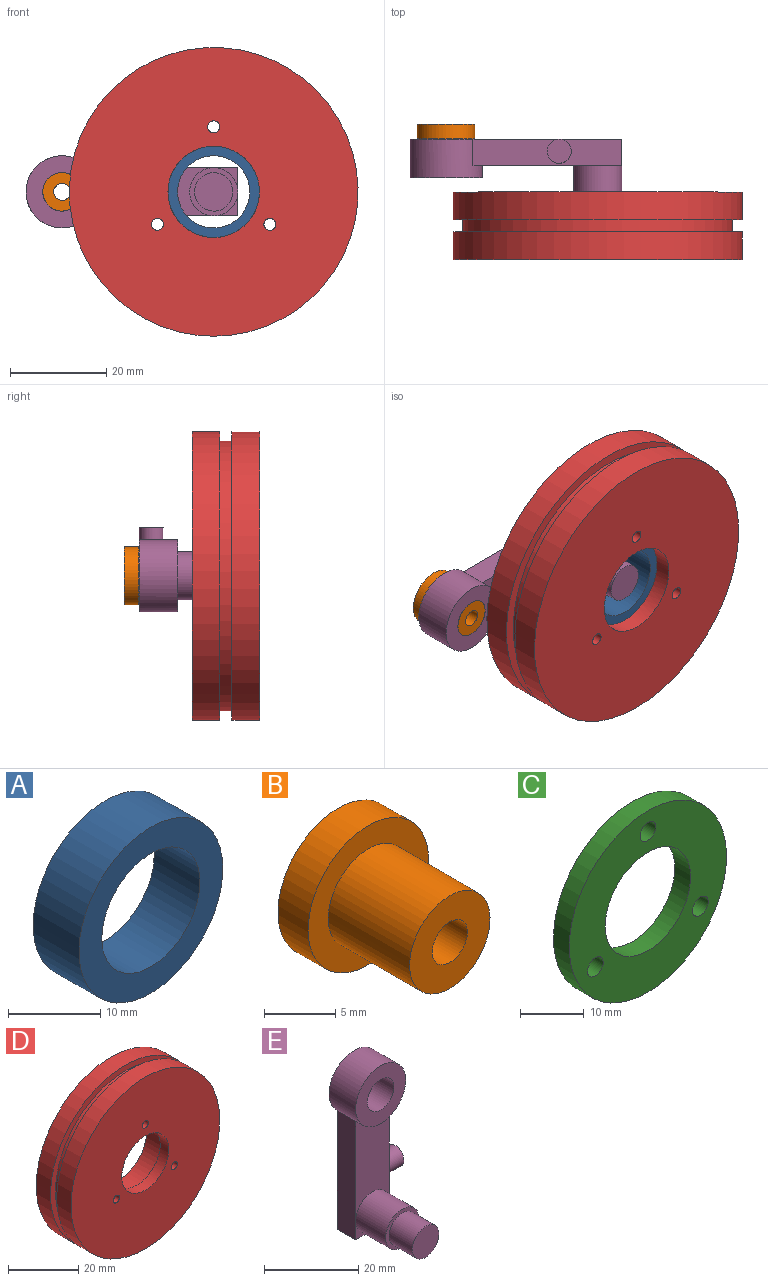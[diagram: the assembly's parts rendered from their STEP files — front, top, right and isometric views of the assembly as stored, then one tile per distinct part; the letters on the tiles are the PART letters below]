
ASSEMBLY  parts=5 mates=7
PART A: 4 faces, bbox 22x7x22 mm
  f0: cylinder r=7.5mm len=15mm, axis (0,1,0), area 329.9mm2, adj f2,f3
  f1: cylinder r=11mm len=22mm, axis (0,1,0), area 483.8mm2, adj f2,f3
  f2: plane 22x22mm, normal (0,-1,0), area 203.4mm2, adj f0,f1
  f3: plane 22x22mm, normal (0,1,0), area 203.4mm2, adj f0,f1
PART B: 6 faces, bbox 12x11.1x12 mm
  f0: cylinder r=4mm len=8.1mm, axis (0,1,0), area 203.6mm2, adj f1,f4
  f1: plane 8x8mm, normal (0,-1,0), area 40.6mm2, adj f0,f5
  f2: cylinder r=6mm len=12mm, axis (0,-1,0), area 113.1mm2, adj f3,f4
  f3: plane 12x12mm, normal (0,1,0), area 103.5mm2, adj f2,f5
  f4: plane 12x12mm, normal (0,-1,0), area 62.8mm2, adj f0,f2
  f5: cylinder r=1.75mm len=11.1mm, axis (0,-1,0), area 122.1mm2, adj f1,f3
PART C: 7 faces, bbox 35x3.5x35 mm
  f0: cylinder r=17.5mm len=35mm, axis (0,1,0), area 384.8mm2, adj f1,f2
  f1: plane 35x35mm, normal (0,-1,0), area 649.7mm2, adj f0,f3,f4,f5,f6
  f2: plane 35x35mm, normal (0,1,0), area 649.7mm2, adj f0,f3,f4,f5,f6
  f3: cylinder r=9.5mm len=19mm, axis (0,-1,0), area 208.9mm2, adj f1,f2
  f4: cylinder r=1.75mm len=3.5mm, axis (0,-1,0), area 38.5mm2, adj f1,f2
  f5: cylinder r=1.75mm len=3.5mm, axis (0,-1,0), area 38.5mm2, adj f1,f2
  f6: cylinder r=1.75mm len=3.5mm, axis (0,-1,0), area 38.5mm2, adj f1,f2
PART D: 15 faces, bbox 60x14x60 mm
  f0: cylinder r=11mm len=22mm, axis (0,1,0), area 483.8mm2, adj f8,f11
  f1: cylinder r=30mm len=60mm, axis (0,1,0), area 1083.8mm2, adj f2,f3
  f2: plane 60x60mm, normal (0,-1,0), area 2529.2mm2, adj f1,f9,f12,f13,f14
  f3: plane 60x60mm, normal (0,1,0), area 364.4mm2, adj f1,f5
  f4: plane 60x60mm, normal (0,-1,0), area 364.4mm2, adj f5,f7
  f5: cylinder r=28mm len=56mm, axis (0,-1,0), area 439.8mm2, adj f3,f4
  f6: plane 60x60mm, normal (0,1,0), area 1865.3mm2, adj f7,f10
  f7: cylinder r=30mm len=60mm, axis (0,1,0), area 1083.8mm2, adj f4,f6
  f8: plane 22x22mm, normal (0,1,0), area 96.6mm2, adj f0,f9
  f9: cylinder r=9.5mm len=19mm, axis (0,1,0), area 208.9mm2, adj f2,f8
  f10: cylinder r=17.5mm len=35mm, axis (0,1,0), area 384.8mm2, adj f6,f11
  f11: plane 35x35mm, normal (0,1,0), area 567.3mm2, adj f0,f10,f12,f13,f14
  f12: cylinder r=1.25mm len=10.5mm, axis (0,1,0), area 82.5mm2, adj f2,f11
  f13: cylinder r=1.25mm len=10.5mm, axis (0,1,0), area 82.5mm2, adj f2,f11
  f14: cylinder r=1.25mm len=10.5mm, axis (0,1,0), area 82.5mm2, adj f2,f11
PART E: 20 faces, bbox 17.5x21.5x44 mm
  f0: plane 10x5.5mm, normal (0,0,-1), area 27mm2, adj f1,f6,f7,f9,f10,f14,f15,f16
  f1: plane 44x15mm, normal (0,1,0), area 212.4mm2, adj f0,f9,f10,f11,f13,f14,f16,f17
  f2: cylinder r=4mm len=8mm, axis (0,1,0), area 175.9mm2, adj f3,f5
  f3: plane 8x8mm, normal (0,-1,0), area 50.3mm2, adj f2
  f4: cylinder r=5mm len=10mm, axis (0,-1,0), area 282.7mm2, adj f5,f6,f7,f8
  f5: plane 10x10mm, normal (0,-1,0), area 28.3mm2, adj f2,f4
  f6: plane 5x5mm, normal (0,-1,0), area 5.4mm2, adj f0,f4,f9
  f7: plane 5x5mm, normal (0,-1,0), area 5.4mm2, adj f0,f4,f10
  f8: plane 25.91x10mm, normal (0,-1,0), area 206.7mm2, adj f4,f9,f10,f11
  f9: plane 30.91x5.5mm, normal (1,0,0), area 150.4mm2, adj f0,f1,f6,f8,f11,f18
  f10: plane 30.91x5.5mm, normal (-1,0,0), area 170mm2, adj f0,f1,f7,f8,f11
  f11: cylinder r=7.5mm len=15mm, axis (0,1,0), area 316.8mm2, adj f1,f8,f9,f10,f12
  f12: plane 15x15mm, normal (0,-1,0), area 126.4mm2, adj f11,f13
  f13: cylinder r=4mm len=8mm, axis (0,1,0), area 201.1mm2, adj f1,f12
  f14: plane 30x4mm, normal (-1,0,0), area 120mm2, adj f0,f1,f15,f17
  f15: plane 30x7mm, normal (0,1,0), area 210mm2, adj f0,f14,f16,f17
  f16: plane 30x4mm, normal (1,0,0), area 120mm2, adj f0,f1,f15,f17
  f17: plane 7x4mm, normal (0,0,-1), area 28mm2, adj f1,f14,f15,f16
  f18: cylinder r=2.5mm len=5mm, axis (-1,0,0), area 78.5mm2, adj f9,f19
  f19: plane 5x5mm, normal (1,0,0), area 19.6mm2, adj f18
PLACE A rot(axis=(0,-1,0),90deg) t=(0.06,3.49,-0.07)mm
PLACE B t=(-31.44,18.09,-0.07)mm
PLACE C t=(0.06,6.99,-0.07)mm
PLACE D t=(0.06,-0.01,-0.07)mm fixed
PLACE E rot(axis=(0,-1,0),90deg) t=(0.06,3.49,-0.07)mm
MATE cylindrical B.f0 <-> E.f11  axis (0,-1,0) through (-31.44,9.99,-0.07)mm
MATE fastened A.f1 <-> D.f0  axis (0,-1,0) through (0.06,-3.51,-0.07)mm
MATE fastened C.f3 <-> D.f1  axis (0,-1,0) through (0.06,3.49,-0.07)mm
MATE fastened E.f2 <-> A.f0  axis (0,-1,0) through (0.06,-3.51,-0.07)mm
MATE fastened B.f0 <-> E.f11  axis (0,-1,0) through (-31.44,9.99,-0.07)mm
MATE cylindrical A.f1 <-> D.f0  axis (0,-1,0) through (0.06,-3.51,-0.07)mm
MATE cylindrical E.f2 <-> A.f0  axis (0,1,0) through (0.06,-3.51,-0.07)mm
